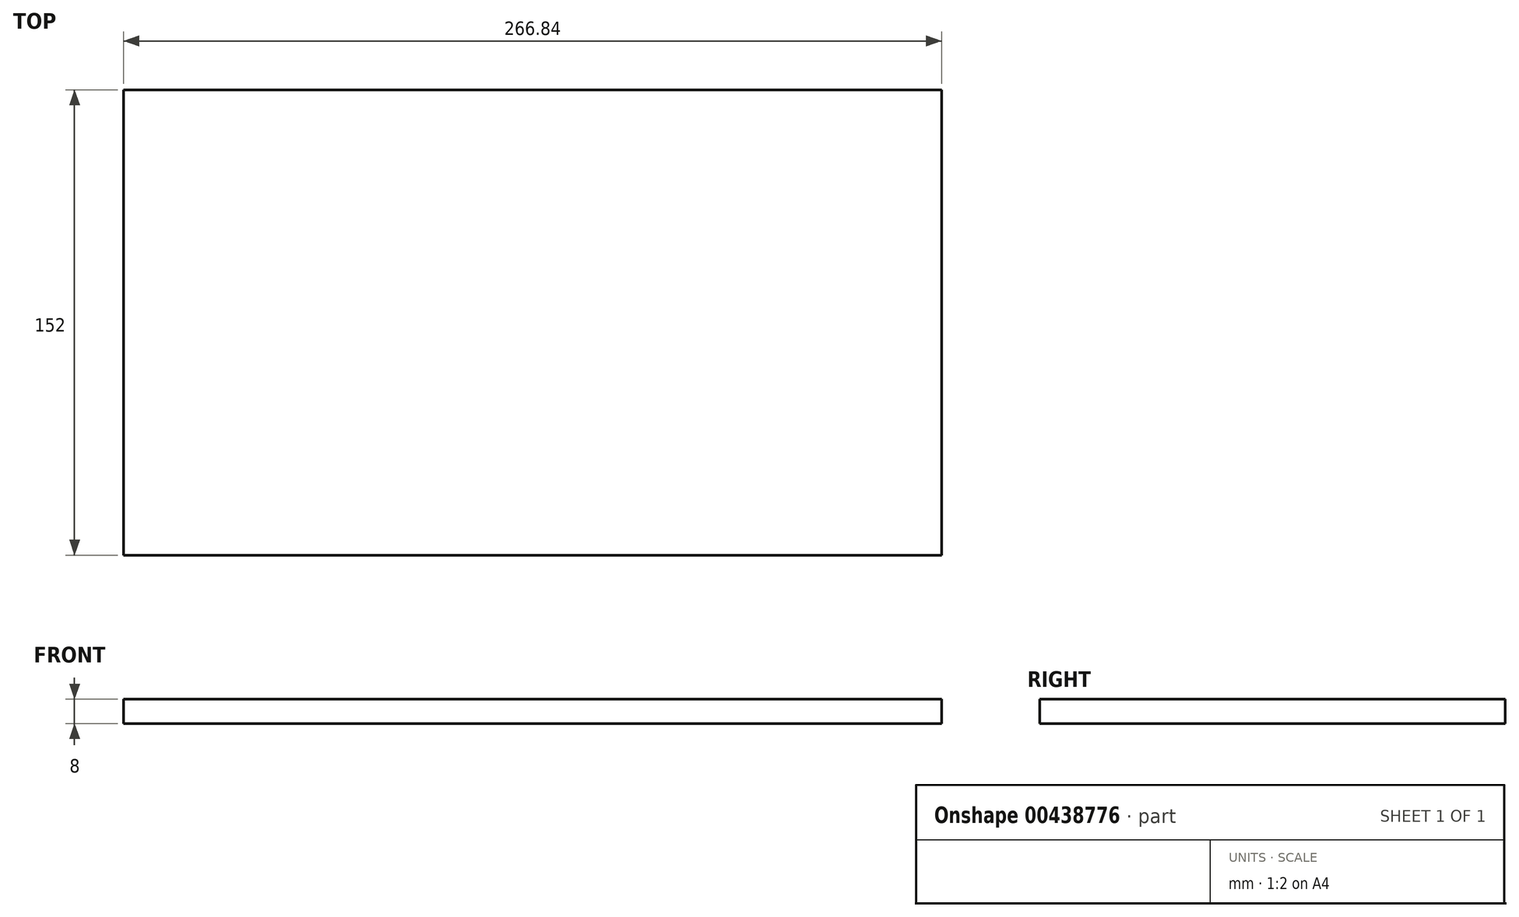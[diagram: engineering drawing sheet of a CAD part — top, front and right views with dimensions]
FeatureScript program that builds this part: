
annotation { "Feature Type Name" : "Feature", "Feature Type Description" : "" }
export const myFeature = defineFeature(function(context is Context, id is Id, definition is map)
    precondition{}
    {
        {
            var Q0;
            Q0=qCreatedBy(makeId("Top.planeOp"),FACE);
            var sketch = newSketch(context, id + "F0", { "sketchPlane" : qUnion([Q0])});
            skLineSegment(sketch, "E0.bottom", {"start": v(133.42, 76) * mm, "end": v(-133.42, 76) * mm});
            skLineSegment(sketch, "E0.top", {"start": v(133.42, -76) * mm, "end": v(-133.42, -76) * mm});
            skLineSegment(sketch, "E0.left", {"start": v(133.42, 76) * mm, "end": v(133.42, -76) * mm});
            skLineSegment(sketch, "E0.right", {"start": v(-133.42, 76) * mm, "end": v(-133.42, -76) * mm});
            skPoint(sketch, "E0.middle", {"position": v(0, 0) * mm});
            skLineSegment(sketch, "E1", {"start": v(-133.42, -76) * mm, "end": v(133.42, 76) * mm, "construction": true});
            skSolve(sketch);
        }
        {
            var Q0;
            Q0=makeQuery(id+"F0.imprint","IMPRINT",FACE,{"disambiguationData":[TD([[makeQuery(id+"F0.imprint","IMPRINT",EDGE,{"derivedFrom":sQuery(id+"F0.wireOp",EDGE,"E0.bottom")}),1.0]])]});
            extrude(context, id + "F1", {"entities" : qUnion([Q0]), "depth" : 8 * mm});
        }
    });
